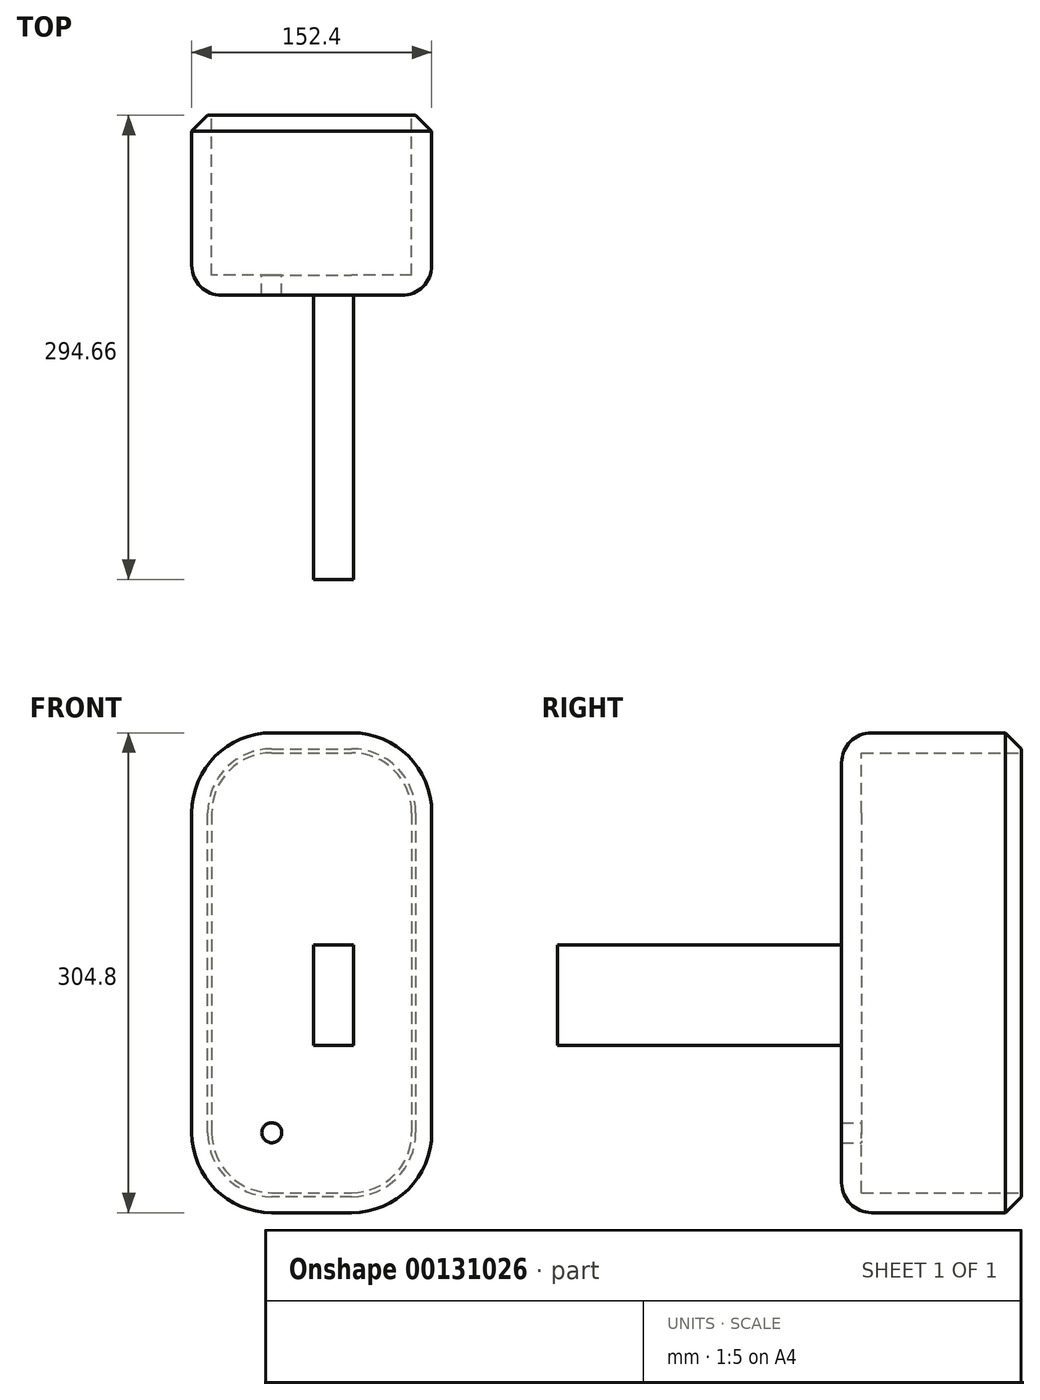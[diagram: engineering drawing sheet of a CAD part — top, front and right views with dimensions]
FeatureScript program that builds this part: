
annotation { "Feature Type Name" : "Feature", "Feature Type Description" : "" }
export const myFeature = defineFeature(function(context is Context, id is Id, definition is map)
    precondition{}
    {
        {
            var Q0;
            Q0=qCreatedBy(makeId("Top.planeOp"),FACE);
            var sketch = newSketch(context, id + "F0", { "sketchPlane" : qUnion([Q0])});
            skLineSegment(sketch, "E0.bottom", {"start": v(0, 0) * mm, "end": v(152.4, 0) * mm});
            skLineSegment(sketch, "E0.top", {"start": v(0, 50.8) * mm, "end": v(152.4, 50.8) * mm});
            skLineSegment(sketch, "E0.left", {"start": v(0, 0) * mm, "end": v(0, 50.8) * mm});
            skLineSegment(sketch, "E0.right", {"start": v(152.4, 0) * mm, "end": v(152.4, 50.8) * mm});
            skSolve(sketch);
        }
        {
            var Q0;
            Q0 = qSketchRegion(id + "F0", true);
            extrude(context, id + "F1", {"entities" : qUnion([Q0]), "depth" : 304.8 * mm});
        }
        {
            var Q0;
            Q0=makeQuery(id+"F1.opExtrude","CAP_EDGE",EDGE,{"disambiguationData":[OSD([sQuery(id+"F0.wireOp",EDGE,"E0.right")])],"isStart":false});
            var Q1;
            Q1=makeQuery(id+"F1.opExtrude","CAP_EDGE",EDGE,{"disambiguationData":[OSD([sQuery(id+"F0.wireOp",EDGE,"E0.right")])],"isStart":true});
            var Q2;
            Q2=makeQuery(id+"F1.opExtrude","CAP_EDGE",EDGE,{"disambiguationData":[OSD([sQuery(id+"F0.wireOp",EDGE,"E0.left")])],"isStart":false});
            var Q3;
            Q3=makeQuery(id+"F1.opExtrude","CAP_EDGE",EDGE,{"disambiguationData":[OSD([sQuery(id+"F0.wireOp",EDGE,"E0.left")])],"isStart":true});
            fillet(context, id + "F2", {"entities" : qUnion([Q0, Q1, Q2, Q3]), "radius" : 50.8 * mm, "tangentPropagation" : true, "allowEdgeOverflow" : false});
        }
        {
            var Q0;
            Q0=makeQuery(id+"F6.imprint","IMPRINT",FACE,{"disambiguationData":[TD([[makeQuery(id+"F6.imprint","IMPRINT",EDGE,{"derivedFrom":sQuery(id+"F6.wireOp",EDGE,"E3.bottom")}),-1.0]])]});
            var Q1;
            Q1=makeQuery(id+"F1.opExtrude","SWEPT_FACE",FACE,{"disambiguationData":[OSD([sQuery(id+"F0.wireOp",EDGE,"E0.bottom")])]});
            extrude(context, id + "F3", {"entities" : qUnion([Q0, Q1]), "operationType" : NewBodyOperationType.ADD, "depth" : 63.5 * mm});
        }
        {
            var Q0;
            Q0=makeQuery(id+"F1.opExtrude","SWEPT_FACE",FACE,{"disambiguationData":[OSD([sQuery(id+"F0.wireOp",EDGE,"E0.top")])]});
            shell(context, id + "F4", {"entities" : qUnion([Q0]), "thickness" : 12.7 * mm});
        }
        {
            var Q0;
            Q0=makeQuery(id+"F1.opExtrude","SWEPT_EDGE",EDGE,{"disambiguationData":[OSD([sQuery(id+"F0.wireOp",EDGE,"E0.bottom"),sQuery(id+"F0.wireOp",EDGE,"E0.left")])]});
            var Q1;
            Q1=makeQuery(id+"F1.opExtrude","SWEPT_EDGE",EDGE,{"disambiguationData":[OSD([sQuery(id+"F0.wireOp",EDGE,"E0.top"),sQuery(id+"F0.wireOp",EDGE,"E0.left")])]});
            chamfer(context, id + "F9", {"entities" : qUnion([Q0, Q1]), "width" : 10.16 * mm, "tangentPropagation" : true});
        }
        {
            var Q0;
            Q0=makeQuery(id+"F1.opExtrude","SWEPT_FACE",FACE,{"disambiguationData":[OSD([sQuery(id+"F0.wireOp",EDGE,"E0.top")])]});
            var sketch = newSketch(context, id + "F10", { "sketchPlane" : qUnion([Q0])});
            skCircle(sketch, "E1", {"center": v(-50.8, 50.8) * mm, "radius": 6.35 * mm});
            skLineSegment(sketch, "E2", {"start": v(0, 44.45) * mm, "end": v(-50.8, 44.45) * mm, "construction": true});
            skSolve(sketch);
        }
        {
            var Q0;
            Q0=makeQuery(id+"F10.imprint","IMPRINT",FACE,{"disambiguationData":[TD([[makeQuery(id+"F10.imprint","IMPRINT",EDGE,{"derivedFrom":sQuery(id+"F10.wireOp",EDGE,"E1")}),1.0]])]});
            extrude(context, id + "F5", {"entities" : qUnion([Q0]), "operationType" : NewBodyOperationType.REMOVE, "endBound" : BoundingType.THROUGH_ALL, "oppositeDirection" : true, "depth" : 99.4 * mm});
        }
        {
            var Q0;
            Q0=makeQuery(id+"F3.opExtrude","CAP_FACE",FACE,{"disambiguationData":[OSD([sQuery(id+"F0.wireOp",EDGE,"E0.bottom")])],"isStart":false});
            var sketch = newSketch(context, id + "F6", { "sketchPlane" : qUnion([Q0])});
            skLineSegment(sketch, "E3.bottom", {"start": v(77.45, 106.38) * mm, "end": v(102.68, 106.38) * mm});
            skLineSegment(sketch, "E3.top", {"start": v(77.45, 169.95) * mm, "end": v(102.68, 169.95) * mm});
            skLineSegment(sketch, "E3.left", {"start": v(77.45, 106.38) * mm, "end": v(77.45, 169.95) * mm});
            skLineSegment(sketch, "E3.right", {"start": v(102.68, 106.38) * mm, "end": v(102.68, 169.95) * mm});
            skSolve(sketch);
        }
        {
            var Q0;
            {var subQ0=sQuery(id+"F0.wireOp",EDGE,"E0.bottom");Q0=makeQuery(id+"F3.opExtrude","CAP_EDGE",EDGE,{"disambiguationData":[OSD([subQ0]),TDD([makeQuery(id+"F6.imprint","IMPRINT",EDGE,{"derivedFrom":makeQuery(id+"F9.opChamfer","BLEND_EDGE",EDGE,{"blendedFrom":[makeQuery(id+"F1.opExtrude","CAP_EDGE",EDGE,{"disambiguationData":[OSD([subQ0])],"isStart":false}),makeQuery(id+"F1.opExtrude","SWEPT_FACE",FACE,{"disambiguationData":[OSD([subQ0])]})],"blendedInto":[makeQuery(id+"F1.opExtrude","SWEPT_FACE",FACE,{"disambiguationData":[OSD([subQ0])]})]})})])],"isStart":false});}
            var Q1;
            {var subQ0=sQuery(id+"F0.wireOp",EDGE,"E0.right");var subQ1=sQuery(id+"F0.wireOp",EDGE,"E0.bottom");Q1=makeQuery(id+"F3.opExtrude","CAP_EDGE",EDGE,{"disambiguationData":[OSD([subQ1,subQ0]),TDD([makeQuery(id+"F1.opExtrude","SWEPT_EDGE",EDGE,{"disambiguationData":[OSD([subQ1,subQ0])]})])],"isStart":false});}
            fillet(context, id + "F7", {"entities" : qUnion([Q0, Q1]), "radius" : 19.05 * mm, "tangentPropagation" : true, "allowEdgeOverflow" : false});
        }
        {
            var Q0;
            Q0=makeQuery(id+"F6.imprint","IMPRINT",FACE,{"disambiguationData":[TD([[makeQuery(id+"F6.imprint","IMPRINT",EDGE,{"derivedFrom":sQuery(id+"F6.wireOp",EDGE,"E3.bottom")}),1.0]])]});
            extrude(context, id + "F11", {"entities" : qUnion([Q0]), "operationType" : NewBodyOperationType.ADD, "depth" : 180.36 * mm});
        }
    });
